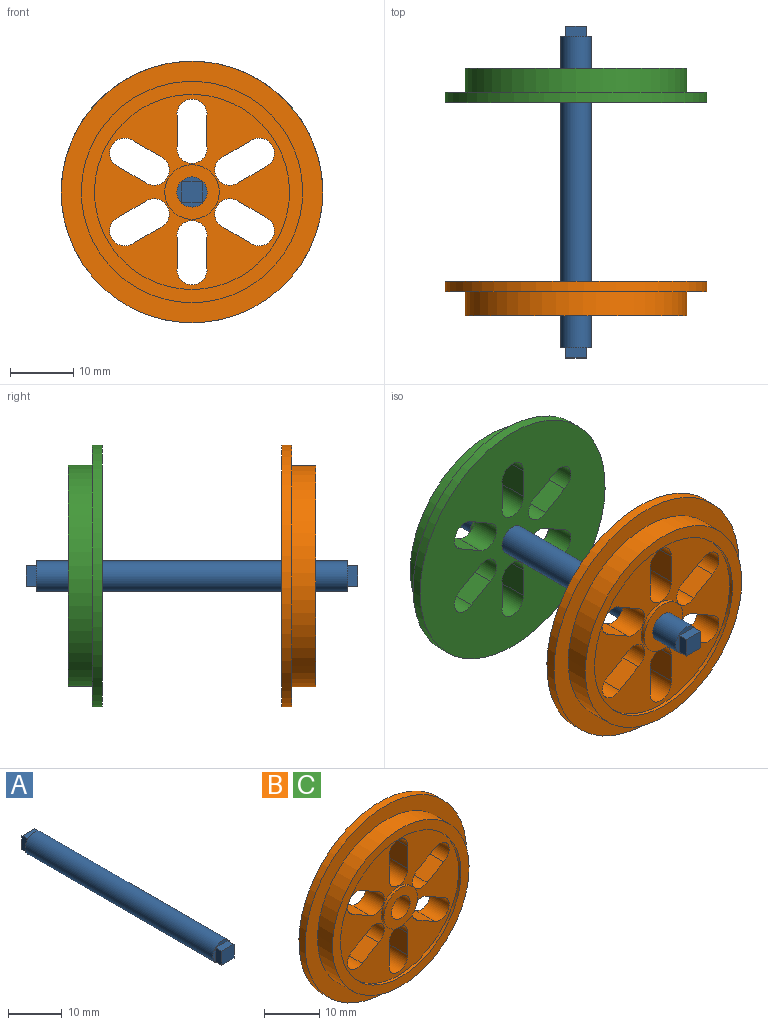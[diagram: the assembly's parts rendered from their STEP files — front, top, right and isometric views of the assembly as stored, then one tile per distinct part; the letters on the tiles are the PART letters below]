
ASSEMBLY  parts=3 mates=2
PART A: 13 faces, bbox 4.8x52.4x4.8 mm
  f0: cylinder r=2.38mm len=49.21mm, axis (0,1,0), area 736.3mm2, adj f1,f7
  f1: plane 4.76x4.76mm, normal (0,1,0), area 7.7mm2, adj f0,f2,f3,f4,f5
  f2: plane 3.18x1.59mm, normal (0,0,-1), area 5mm2, adj f1,f3,f5,f6
  f3: plane 3.18x1.59mm, normal (-1,0,0), area 5mm2, adj f1,f2,f4,f6
  f4: plane 3.18x1.59mm, normal (0,0,1), area 5mm2, adj f1,f3,f5,f6
  f5: plane 3.18x1.59mm, normal (1,0,0), area 5mm2, adj f1,f2,f4,f6
  f6: plane 3.18x3.18mm, normal (0,1,0), area 10.1mm2, adj f2,f3,f4,f5
  f7: plane 4.76x4.76mm, normal (0,-1,0), area 7.7mm2, adj f0,f8,f9,f10,f11
  f8: plane 3.18x1.59mm, normal (0,0,-1), area 5mm2, adj f7,f9,f11,f12
  f9: plane 3.18x1.59mm, normal (-1,0,0), area 5mm2, adj f7,f8,f10,f12
  f10: plane 3.18x1.59mm, normal (0,0,1), area 5mm2, adj f7,f9,f11,f12
  f11: plane 3.18x1.59mm, normal (1,0,0), area 5mm2, adj f7,f8,f10,f12
  f12: plane 3.18x3.18mm, normal (0,-1,0), area 10.1mm2, adj f8,f9,f10,f11
PART B: 34 faces, bbox 41.3x5.4x41.3 mm
  f0: cylinder r=20.64mm len=41.28mm, axis (0,1,0), area 205.8mm2, adj f1,f2
  f1: plane 41.28x41.28mm, normal (0,-1,0), area 380mm2, adj f0,f4
  f2: plane 41.28x41.28mm, normal (0,1,0), area 1061.6mm2, adj f0,f7,f10,f11,f12,f13,f14,f15
  f3: cylinder r=15.39mm len=30.78mm, axis (0,1,0), area 60.2mm2, adj f5,f6
  f4: cylinder r=17.46mm len=34.93mm, axis (0,1,0), area 416.6mm2, adj f1,f5
  f5: plane 34.93x34.93mm, normal (0,-1,0), area 213.8mm2, adj f3,f4
  f6: plane 30.78x30.78mm, normal (0,-1,0), area 427.4mm2, adj f3,f8,f10,f11,f12,f13,f14,f15
  f7: cylinder r=2.38mm len=5.39mm, axis (0,1,0), area 80.6mm2, adj f2,f9
  f8: cylinder r=4.3mm len=8.61mm, axis (0,1,0), area 16.8mm2, adj f6,f9
  f9: plane 8.61x8.61mm, normal (0,-1,0), area 40.4mm2, adj f7,f8
  f10: cylinder r=2.37mm len=4.76mm, axis (0,-1,0), area 37.7mm2, adj f2,f6,f11,f13
  f11: plane 4.91x4.76mm, normal (-1,0,0), area 23.4mm2, adj f2,f6,f10,f12
  f12: cylinder r=2.37mm len=4.76mm, axis (0,-1,0), area 37.7mm2, adj f2,f6,f11,f13
  f13: plane 4.91x4.76mm, normal (1,0,0), area 23.4mm2, adj f2,f6,f10,f12
  f14: cylinder r=2.37mm len=4.76mm, axis (0,-1,0), area 37.7mm2, adj f2,f6,f15,f17
  f15: plane 4.76x4.25mm, normal (-0.5,0,0.87), area 23.4mm2, adj f2,f6,f14,f16
  f16: cylinder r=2.37mm len=4.76mm, axis (0,-1,0), area 37.7mm2, adj f2,f6,f15,f17
  f17: plane 4.76x4.25mm, normal (0.5,0,-0.87), area 23.4mm2, adj f2,f6,f14,f16
  f18: cylinder r=2.37mm len=4.76mm, axis (0,-1,0), area 37.7mm2, adj f2,f6,f19,f21
  f19: plane 4.76x4.25mm, normal (0.5,0,0.87), area 23.4mm2, adj f2,f6,f18,f20
  f20: cylinder r=2.37mm len=4.76mm, axis (0,-1,0), area 37.7mm2, adj f2,f6,f19,f21
  f21: plane 4.76x4.25mm, normal (-0.5,0,-0.87), area 23.4mm2, adj f2,f6,f18,f20
  f22: cylinder r=2.37mm len=4.76mm, axis (0,-1,0), area 37.7mm2, adj f2,f6,f23,f25
  f23: plane 4.91x4.76mm, normal (1,0,0), area 23.4mm2, adj f2,f6,f22,f24
  f24: cylinder r=2.37mm len=4.76mm, axis (0,-1,0), area 37.7mm2, adj f2,f6,f23,f25
  f25: plane 4.91x4.76mm, normal (-1,0,0), area 23.4mm2, adj f2,f6,f22,f24
  f26: cylinder r=2.37mm len=4.76mm, axis (0,-1,0), area 37.7mm2, adj f2,f6,f27,f29
  f27: plane 4.76x4.25mm, normal (0.5,0,-0.87), area 23.4mm2, adj f2,f6,f26,f28
  f28: cylinder r=2.37mm len=4.76mm, axis (0,-1,0), area 37.7mm2, adj f2,f6,f27,f29
  f29: plane 4.76x4.25mm, normal (-0.5,0,0.87), area 23.4mm2, adj f2,f6,f26,f28
  f30: cylinder r=2.37mm len=4.76mm, axis (0,-1,0), area 37.7mm2, adj f2,f6,f31,f33
  f31: plane 4.76x4.25mm, normal (-0.5,0,-0.87), area 23.4mm2, adj f2,f6,f30,f32
  f32: cylinder r=2.37mm len=4.76mm, axis (0,-1,0), area 37.7mm2, adj f2,f6,f31,f33
  f33: plane 4.76x4.25mm, normal (0.5,0,0.87), area 23.4mm2, adj f2,f6,f30,f32
PART C: same geometry as B
PLACE A t=(0.68,24.33,-3.38)mm
PLACE B t=(0.68,-16,-3.38)mm
PLACE C rot(axis=(1,0,0),180deg) t=(0.68,12.28,-3.38)mm
MATE fastened B.f7 <-> A.f0  axis (0,1,0) through (0.68,-21.39,-3.38)mm
MATE fastened C.f8 <-> A.f0  axis (0,1,0) through (0.68,17.66,-3.38)mm
